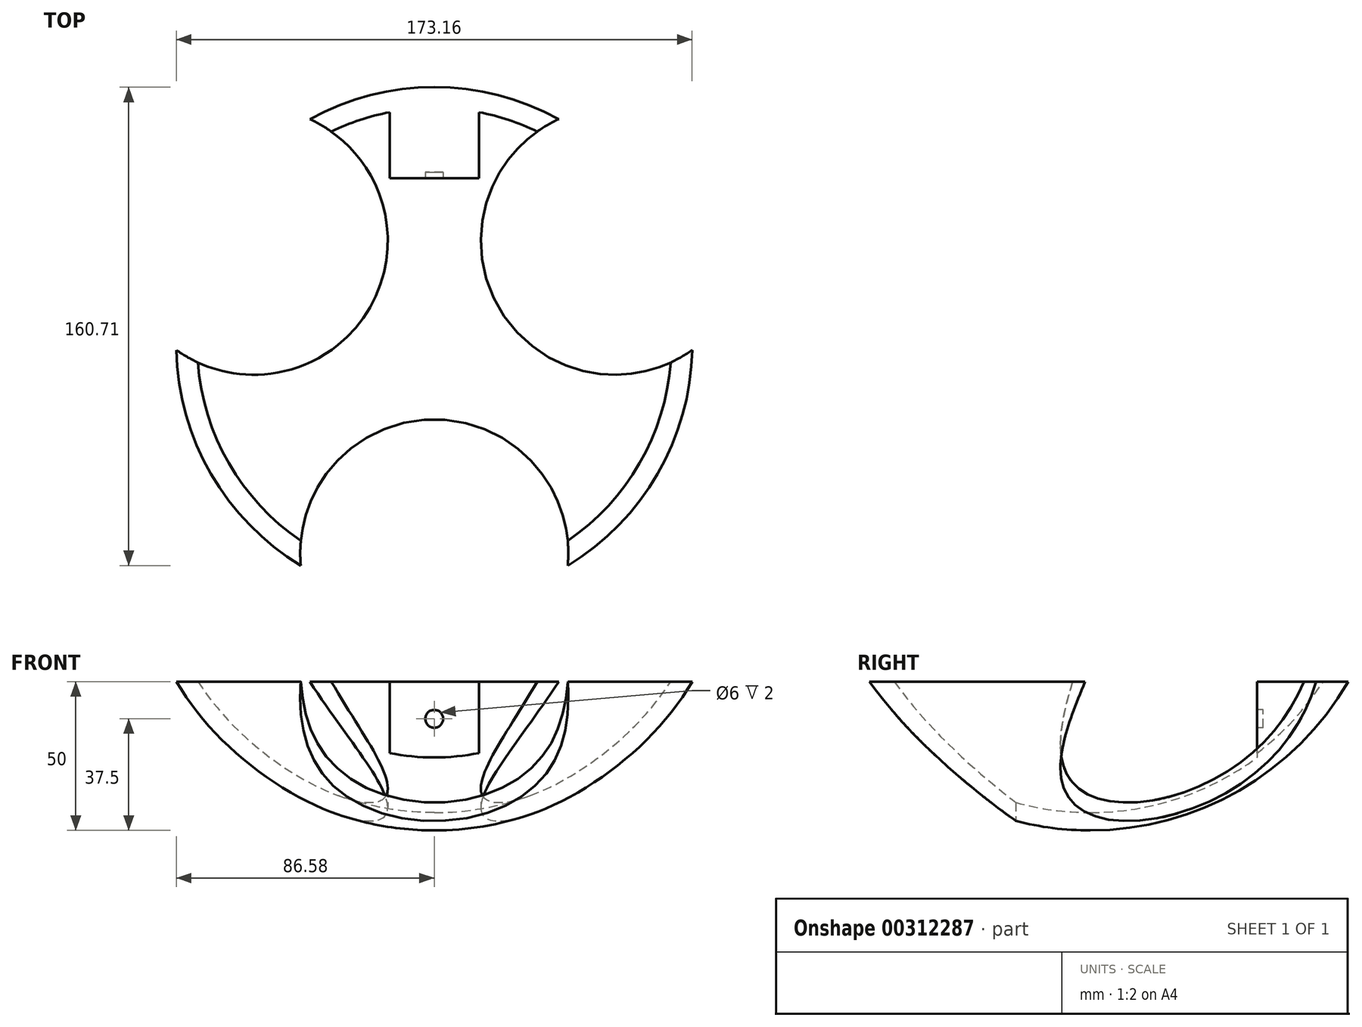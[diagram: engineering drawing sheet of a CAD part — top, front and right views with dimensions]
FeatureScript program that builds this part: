
annotation { "Feature Type Name" : "Feature", "Feature Type Description" : "" }
export const myFeature = defineFeature(function(context is Context, id is Id, definition is map)
    precondition{}
    {
        {
            var Q0;
            Q0=qCreatedBy(makeId("Front.planeOp"),FACE);
            var sketch = newSketch(context, id + "F0", { "sketchPlane" : qUnion([Q0])});
            skArc(sketch, "E0", {"start": v(-86.6, -50) * mm, "mid": v(-50, -86.6) * mm, "end": v(0, -100) * mm});
            skLineSegment(sketch, "E1", {"start": v(0, -50) * mm, "end": v(0, -100) * mm});
            skLineSegment(sketch, "E2", {"start": v(0, -50) * mm, "end": v(-86.6, -50) * mm});
            skPoint(sketch, "E3.orphan", {"position": v(0, 100) * mm});
            skSolve(sketch);
        }
        {
            var Q0;
            Q0=makeQuery(id+"F0.imprint","IMPRINT",FACE,{"disambiguationData":[TD([[makeQuery(id+"F0.imprint","IMPRINT",EDGE,{"derivedFrom":sQuery(id+"F0.wireOp",EDGE,"E0")}),1.0]])]});
            var Q1;
            Q1=sQuery(id+"F0.wireOp",EDGE,"E1");
            revolve(context, id + "F1", {"entities" : qUnion([Q0]), "axis" : qUnion([Q1]), "revolveType" : RevolveType.FULL});
        }
        {
            var Q0;
            Q0=makeQuery(id+"F1.opRevolve","SWEPT_FACE",FACE,{"disambiguationData":[OSD([sQuery(id+"F0.wireOp",EDGE,"E2")])]});
            shell(context, id + "F2", {"entities" : qUnion([Q0]), "thickness" : 6 * mm});
        }
        {
            var Q0;
            Q0=qCreatedBy(makeId("Front.planeOp"),FACE);
            cPlane(context, id + "F3", {"entities" : qUnion([Q0]), "cplaneType" : CPlaneType.OFFSET, "offset" : 56 * mm, "oppositeDirection" : true, "width" : 150 * mm, "height" : 150 * mm});
        }
        {
            var Q0;
            Q0=qCreatedBy(id+"F3.planeOp",FACE);
            var sketch = newSketch(context, id + "F4", { "sketchPlane" : qUnion([Q0])});
            skLineSegment(sketch, "E4.0", {"start": v(-15, -50) * mm, "end": v(15, -50) * mm});
            skLineSegment(sketch, "E5", {"start": v(-15, -50) * mm, "end": v(-15, -90) * mm});
            skLineSegment(sketch, "E6", {"start": v(-15, -90) * mm, "end": v(15, -90) * mm});
            skLineSegment(sketch, "E7", {"start": v(15, -90) * mm, "end": v(15, -50) * mm});
            skPoint(sketch, "E8.orphan", {"position": v(86.6, -50) * mm});
            skPoint(sketch, "E9.orphan", {"position": v(-86.6, -50) * mm});
            skSolve(sketch);
        }
        {
            var Q0;
            Q0=qSketchRegion(id+"F4",true);
            var Q1;
            Q1=makeQuery(id+"F2.opShell","OFFSET_FACE",FACE,{"disambiguationData":[OSD([sQuery(id+"F0.wireOp",EDGE,"E0")])]});
            extrude(context, id + "F5", {"entities" : qUnion([Q0]), "operationType" : NewBodyOperationType.ADD, "endBound" : BoundingType.UP_TO_SURFACE, "oppositeDirection" : true, "endBoundEntityFace" : qUnion([Q1]), "depth" : 25 * mm});
        }
        {
            var Q0;
            Q0=makeQuery(id+"F5.opExtrude","CAP_FACE",FACE,{"disambiguationData":[OSD([sQuery(id+"F4.wireOp",EDGE,"E4.0"),sQuery(id+"F4.wireOp",EDGE,"E5"),sQuery(id+"F4.wireOp",EDGE,"E6"),sQuery(id+"F4.wireOp",EDGE,"E7")])],"isStart":true});
            var sketch = newSketch(context, id + "F6", { "sketchPlane" : qUnion([Q0])});
            skCircle(sketch, "E10", {"center": v(0, -62.5) * mm, "radius": 3 * mm});
            skSolve(sketch);
        }
        {
            var Q0;
            Q0=qSketchRegion(id+"F6",true);
            extrude(context, id + "F7", {"entities" : qUnion([Q0]), "operationType" : NewBodyOperationType.REMOVE, "oppositeDirection" : true, "depth" : 2 * mm});
        }
        {
            var Q0;
            Q0=qCreatedBy(makeId("Top.planeOp"),FACE);
            cPlane(context, id + "F8", {"entities" : qUnion([Q0]), "cplaneType" : CPlaneType.OFFSET, "offset" : 100 * mm, "oppositeDirection" : true, "width" : 150 * mm, "height" : 150 * mm});
        }
        {
            var Q0;
            Q0=qCreatedBy(id+"F8.planeOp",FACE);
            var sketch = newSketch(context, id + "F9", { "sketchPlane" : qUnion([Q0])});
            skLineSegment(sketch, "E11", {"start": v(0, 0) * mm, "end": v(0, -140) * mm, "construction": true});
            skLineSegment(sketch, "E12", {"start": v(0, 0) * mm, "end": v(121.24, 70) * mm, "construction": true});
            skLineSegment(sketch, "E13", {"start": v(0, 0) * mm, "end": v(-121.24, 70) * mm, "construction": true});
            skArc(sketch, "E14", {"start": v(44.81, -74.1) * mm, "mid": v(0, -25) * mm, "end": v(-44.81, -74.1) * mm});
            skArc(sketch, "E15", {"start": v(41.77, 75.86) * mm, "mid": v(21.65, 12.5) * mm, "end": v(86.58, -1.75) * mm});
            skArc(sketch, "E16", {"start": v(-86.58, -1.75) * mm, "mid": v(-21.65, 12.5) * mm, "end": v(-41.77, 75.86) * mm});
            skArc(sketch, "E17.0", {"start": v(-44.81, -74.1) * mm, "mid": v(0, -86.6) * mm, "end": v(44.81, -74.1) * mm});
            skArc(sketch, "E18.trimOffspring", {"start": v(86.58, -1.75) * mm, "mid": v(75, 43.3) * mm, "end": v(41.77, 75.86) * mm});
            skArc(sketch, "E19.trimOffspring", {"start": v(-41.77, 75.86) * mm, "mid": v(-75, 43.3) * mm, "end": v(-86.58, -1.75) * mm});
            skSolve(sketch);
        }
        {
            var Q0;
            Q0=qSketchRegion(id+"F9",true);
            extrude(context, id + "F10", {"entities" : qUnion([Q0]), "operationType" : NewBodyOperationType.REMOVE, "depth" : 100 * mm});
        }
    });
